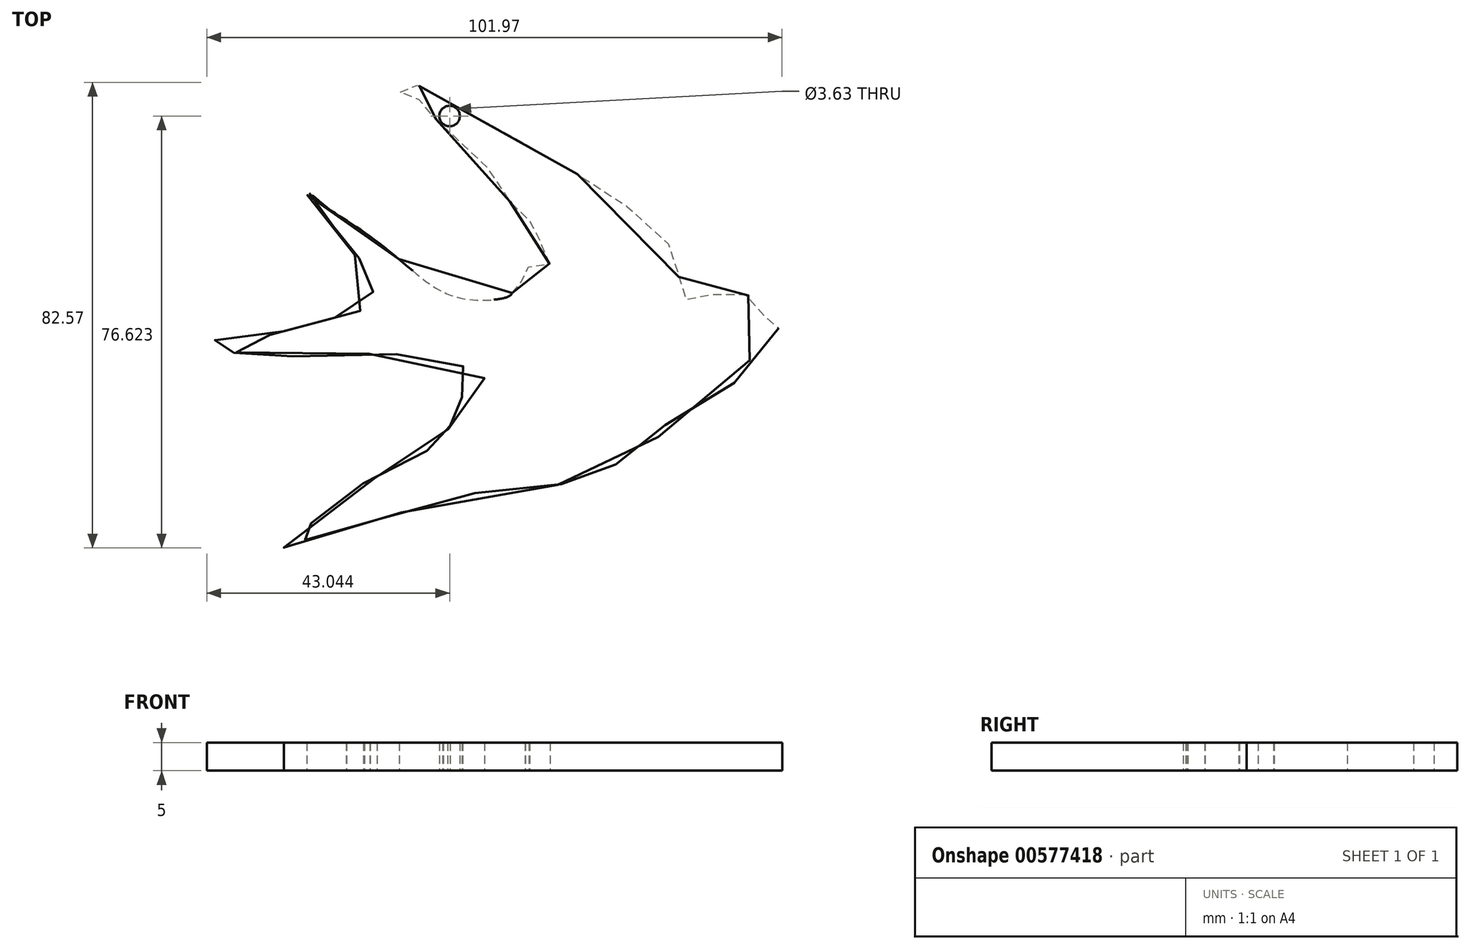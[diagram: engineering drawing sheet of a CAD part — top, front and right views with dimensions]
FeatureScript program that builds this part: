
annotation { "Feature Type Name" : "Feature", "Feature Type Description" : "" }
export const myFeature = defineFeature(function(context is Context, id is Id, definition is map)
    precondition{}
    {
        {
            var Q0;
            Q0=qCreatedBy(makeId("Top.planeOp"),FACE);
            var sketch = newSketch(context, id + "F0", { "sketchPlane" : qUnion([Q0])});
            skFitSpline(sketch, "E0", {"points": [v(-22.51, -3.98) * mm, v(-22.3, -2.38) * mm, v(-21.45, -1.95) * mm, v(-20.27, -1.74) * mm, v(-20.17, 0) * mm, v(-18.56, 0.93) * mm, v(-15.79, 0.93) * mm, v(-17.18, 2.96) * mm, v(-17.71, 5.63) * mm, v(-19.42, 7.23) * mm, v(-19.53, 9.9) * mm, v(-22.4, 11.82) * mm, v(-26.57, 17.8) * mm, v(-29.77, 21.21) * mm, v(-34.47, 25.06) * mm, v(-37.36, 28.69) * mm, v(-39.17, 30.4) * mm, v(-41.1, 30.71) * mm, v(-42.48, 31.89) * mm, v(-41.84, 33.28) * mm, v(-35.11, 30.71) * mm, v(-20.27, 22.5) * mm, v(-6.4, 14.27) * mm, v(5.14, 4.77) * mm, v(6.85, 0) * mm, v(7.38, -2.8) * mm, v(8.55, -5.26) * mm, v(11.33, -4.62) * mm, v(15.17, -3.98) * mm, v(20.3, -4.94) * mm, v(22.54, -8.36) * mm, v(25.32, -9.43) * mm, v(22.97, -11.56) * mm, v(18.59, -17.43) * mm, v(13.04, -23.3) * mm, v(4.5, -27.47) * mm, v(3.32, -29.6) * mm, v(-3.72, -34.2) * mm, v(-6.6, -35.16) * mm, v(-9.6, -36.86) * mm, v(-21.77, -38.68) * mm, v(-29.99, -39.64) * mm, v(-44.08, -43.48) * mm, v(-51.34, -45.51) * mm, v(-60.3, -48.18) * mm, v(-62.98, -49.14) * mm, v(-59.03, -45.4) * mm, v(-51.77, -40.7) * mm, v(-49.42, -38.04) * mm, v(-40.77, -34.52) * mm, v(-37.36, -31.85) * mm, v(-34.8, -30.67) * mm, v(-34.8, -28.86) * mm, v(-33.51, -27.8) * mm, v(-33.94, -26.08) * mm, v(-32.44, -24.05) * mm, v(-31.27, -23.73) * mm, v(-31.27, -21.81) * mm, v(-27.43, -19.25) * mm, v(-30.63, -17.22) * mm, v(-34.05, -15.83) * mm, v(-42.16, -14.87) * mm, v(-57.32, -14.98) * mm, v(-65, -14.98) * mm, v(-65.43, -14.55) * mm, v(-73.01, -14.55) * mm, v(-75.04, -14.34) * mm, v(-76.54, -14.02) * mm, v(-76.11, -12.84) * mm, v(-67.89, -11.35) * mm, v(-63.09, -10.92) * mm, v(-62.77, -9.85) * mm, v(-58.28, -9.32) * mm, v(-51.88, -7.72) * mm, v(-47.71, -6.01) * mm, v(-47.6, -3.98) * mm, v(-46.43, -3.56) * mm, v(-48.78, -0.89) * mm, v(-48.78, 1.36) * mm, v(-51.88, 3.92) * mm, v(-51.88, 4.88) * mm, v(-53.48, 6.59) * mm, v(-54.97, 9.26) * mm, v(-58.17, 12.24) * mm, v(-58.81, 13.85) * mm, v(-55.72, 11.5) * mm, v(-49.95, 7.65) * mm, v(-42.16, 1.68) * mm, v(-33.83, -4.2) * mm, v(-25.82, -5.16) * mm, v(-22.51, -3.98) * mm]});
            skCircle(sketch, "E1", {"center": v(-33.6, 27.43) * mm, "radius": 1.82 * mm});
            skSolve(sketch);
        }
        {
            var Q0;
            Q0 = qSketchRegion(id + "F0", true);
            extrude(context, id + "F1", {"entities" : qUnion([Q0]), "depth" : 5 * mm, "offsetDistance" : 25 * mm});
        }
        {
            var Q0;
            Q0=sQuery(id+"F0.wireOp",EDGE,"E1");
            extrude(context, id + "F2", {"bodyType" : ToolBodyType.SURFACE, "surfaceEntities" : qUnion([Q0]), "depth" : 5.3 * mm, "offsetDistance" : 25 * mm});
        }
    });
